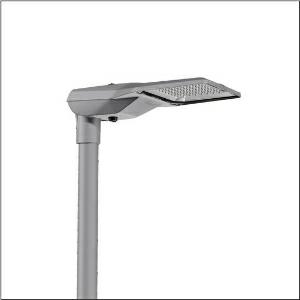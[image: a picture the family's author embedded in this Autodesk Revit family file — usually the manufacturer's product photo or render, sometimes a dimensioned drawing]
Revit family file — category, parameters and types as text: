
# Revit family: streetlight_sl_21_midi___st0_8a_5xe3c33t08lb_3015
name_source: partatom
category: Lighting Fixtures
units: mm (PartAtom-declared; Revit-internal decimal feet)

## family parameters
Cut with Voids When Loaded = No
Host = Face
Light Source = No
Part Type = Normal
Room Calculation Point = No
Round Connector Dimension = Use Diameter
Shared = No

## types (1)
- --- (1 x LED, 14340 lm, 99.6 W, 3000K)
    Apparent Load = 100 VA
    CIE Flux Codes = 38 75 97 100 100
    Color Rendering = 70
    Color Temperature = 3000K
    Default Elevation = 1800 mm
    Description = Streetlight SL 21 midi, mast luminaire, primary light control with lens, of PMMA, primary optical cover: cover, of toughened safety glass, transparent, light distribution: ST0.8a, light emission: direct distribution, primary light characteristic: asymmetric, installation type: side-entry, post-top, LED, High Power LED, rated luminous flux: 14.340lm, luminous efficacy: 144lm/W, light colour: 730, colour temperature: 3000K, control gear: D4i, control: overheat protection, constant luminous flux control, time-dependent luminous flux control, flexible luminous flux parameterisation, pre-setting: logarithmic dimming characteristic, mains connection: 230..240V, AC, 50/60Hz, start of lifetime: 100W, end of service life: 102W, reduction: 46W, luminaire housing, of diecast aluminium, powder-coated, SITECO metallic grey (DB 702S), corrosivity category C5 high according to DIN EN ISO 12944, please order mast flange separately, inclination adjustable: 0°, 5°, 10°, 15°, sealing non-destructively replaceable, multi-level sealing system, length: 644mm, width: 335mm, height: 110mm, mast flange for spigot size: 42mm (side-entry): 5XC10008XM4, 60/48mm (side-entry/post-top): 5XC10108XM2, 76/60mm (side-entry/post-top): 5XC10108XM1, mounting height: 4..8m, Smart Interface below and above, protection rating (complete): IP66, insulation class (complete): insulation class II (safety insulation), certification: CE, ENEC, ENEC+, VDE, impact resistance: IK10, permissible operating ambient temperature for outdoor applications: -40..+50°C, standard-compliant lighting for roads and squares, packaging unit: 1 piece

Light Distribution: ST0.8a
    Height = 111 mm
    Lamp = 1 x LED
    Lamp Light Flux = 14340 lm
    Lamp Power = 99.6 W
    Lamp count = 1
    Length = 644 mm
    Luminous efficacy = 144 lm/W
    Manufacturer = Siteco
    ModVariant = No
    Model = 5XE3C33T08LB
    Number of Poles = 1
    OnlyDefault = Yes
    Power Factor = 1
    Product Name = Streetlight SL 21 midi | ST0.8a
    Product group = mast luminaire | pylon top
    ProductGroupID = 6100
    Protection Class = Protection class II
    Protection Degree = IP 66
    RLX_Detail_Level = 1
    RLX_Emergency_Light_Flux = 0 lm
    RLX_Emergency_Type = 0
    RLX_Emergency_Type_DB = No
    RlxData = <blob elided: 26997 chars, md5=9138a5ef>
    Socket = socket
    Standby Power = 0 W
    System Light Flux = 14340 lm
    System Power = 100 W
    Type Comments = factory setting: luminous flux: 100 % | dim-lin: 254 | 1020 mA
    Type Image = l_1004304.jpg
    URL = http://relux.com
    VarID = @adj_030855
    Voltage = 0 V
    Weight = 0.00 kg
    Width = 336 mm

## geometry (parser evidence)
native form markers: Blend x4, Sweep x10
no freeform markers — native parametric forms only
